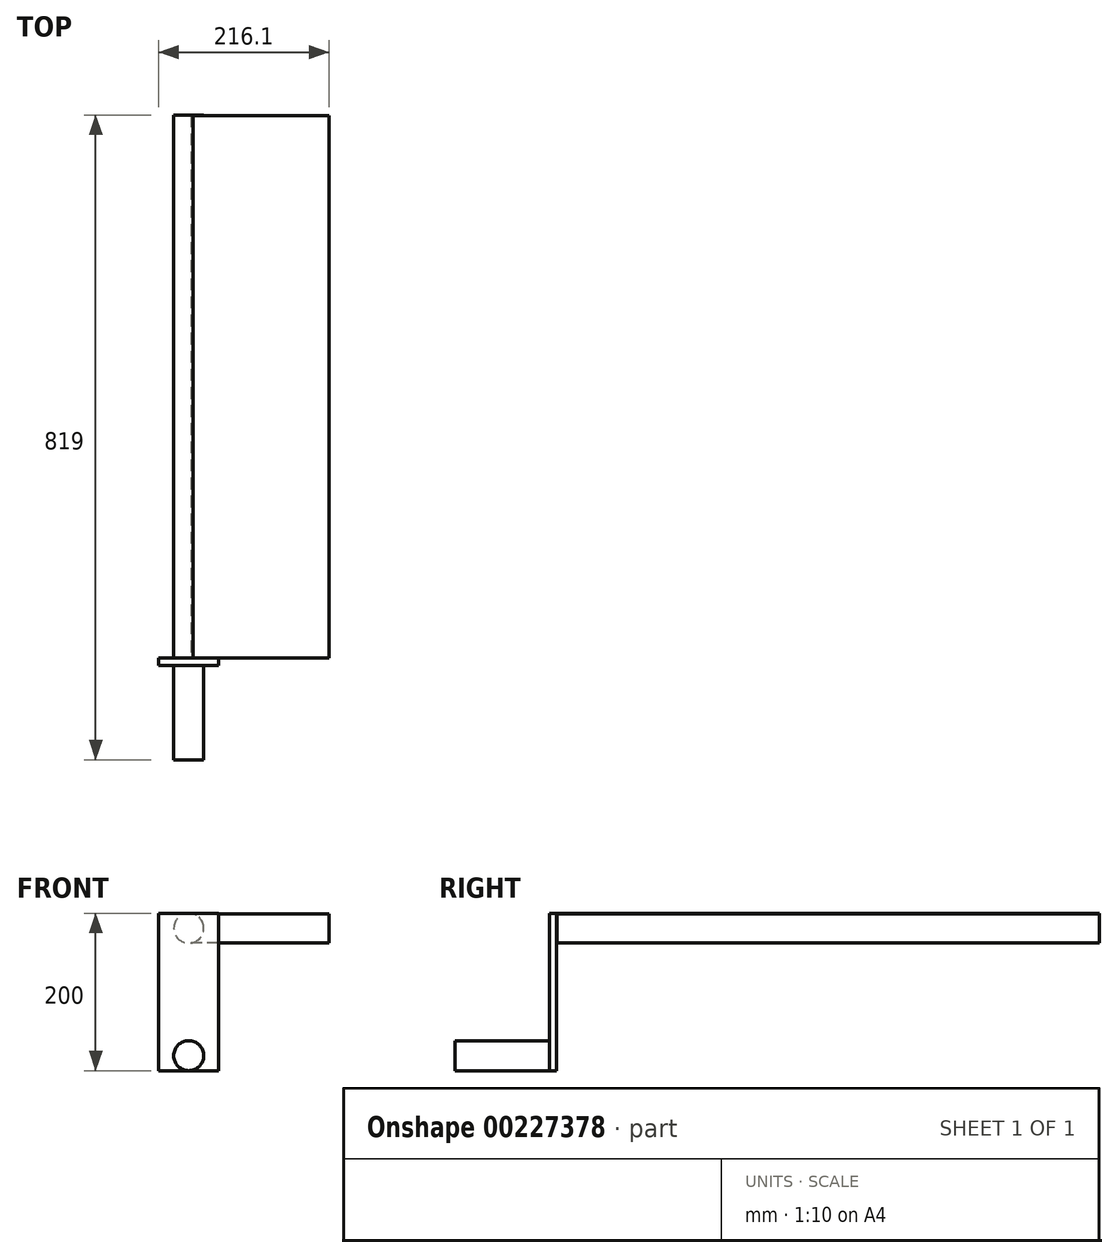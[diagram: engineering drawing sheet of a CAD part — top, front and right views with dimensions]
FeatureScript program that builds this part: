
annotation { "Feature Type Name" : "Feature", "Feature Type Description" : "" }
export const myFeature = defineFeature(function(context is Context, id is Id, definition is map)
    precondition{}
    {
        {
            var Q0;
            Q0=qCreatedBy(makeId("Front.planeOp"),FACE);
            var sketch = newSketch(context, id + "F0", { "sketchPlane" : qUnion([Q0])});
            skLineSegment(sketch, "E0.bottom", {"start": v(38.1, -100) * mm, "end": v(-38.1, -100) * mm});
            skLineSegment(sketch, "E0.top", {"start": v(38.1, 100) * mm, "end": v(-38.1, 100) * mm});
            skLineSegment(sketch, "E0.left", {"start": v(38.1, -100) * mm, "end": v(38.1, 100) * mm});
            skLineSegment(sketch, "E0.right", {"start": v(-38.1, -100) * mm, "end": v(-38.1, 100) * mm});
            skPoint(sketch, "E0.middle", {"position": v(0, 0) * mm});
            skSolve(sketch);
        }
        {
            var Q0;
            Q0 = qSketchRegion(id + "F0", true);
            extrude(context, id + "F1", {"entities" : qUnion([Q0]), "endBound" : BoundingType.SYMMETRIC, "depth" : 9 * mm});
        }
        {
            var Q0;
            Q0=makeQuery(id+"F1.opExtrude","CAP_FACE",FACE,{"disambiguationData":[OSD([sQuery(id+"F0.wireOp",EDGE,"E0.bottom"),sQuery(id+"F0.wireOp",EDGE,"E0.top"),sQuery(id+"F0.wireOp",EDGE,"E0.left"),sQuery(id+"F0.wireOp",EDGE,"E0.right")])],"isStart":false});
            var sketch = newSketch(context, id + "F2", { "sketchPlane" : qUnion([Q0])});
            skPoint(sketch, "E1.centerSnap0", {"position": v(0, -100) * mm});
            skCircle(sketch, "E2", {"center": v(0, -80.95) * mm, "radius": 19.05 * mm});
            skSolve(sketch);
        }
        {
            var Q0;
            Q0 = qSketchRegion(id + "F2", true);
            extrude(context, id + "F3", {"entities" : qUnion([Q0]), "operationType" : NewBodyOperationType.ADD, "depth" : 120 * mm});
        }
        {
            var Q0;
            Q0=makeQuery(id+"F1.opExtrude","CAP_FACE",FACE,{"disambiguationData":[OSD([sQuery(id+"F0.wireOp",EDGE,"E0.bottom"),sQuery(id+"F0.wireOp",EDGE,"E0.top"),sQuery(id+"F0.wireOp",EDGE,"E0.left"),sQuery(id+"F0.wireOp",EDGE,"E0.right")])],"isStart":true});
            var sketch = newSketch(context, id + "F4", { "sketchPlane" : qUnion([Q0])});
            skCircle(sketch, "E3", {"center": v(0, 81) * mm, "radius": 19 * mm});
            skPoint(sketch, "E3.centerSnap0", {"position": v(0, 100) * mm});
            skSolve(sketch);
        }
        {
            var Q0;
            Q0 = qSketchRegion(id + "F4", true);
            extrude(context, id + "F5", {"entities" : qUnion([Q0]), "operationType" : NewBodyOperationType.ADD, "depth" : 690 * mm});
        }
        {
            var Q0;
            Q0=qCreatedBy(makeId("Right.planeOp"),FACE);
            var sketch = newSketch(context, id + "F6", { "sketchPlane" : qUnion([Q0])});
            skLineSegment(sketch, "E4.bottom", {"start": v(5.02, 62.25) * mm, "end": v(693.98, 62.25) * mm});
            skLineSegment(sketch, "E4.top", {"start": v(5.02, 99.24) * mm, "end": v(693.98, 99.24) * mm});
            skLineSegment(sketch, "E4.left", {"start": v(5.02, 62.25) * mm, "end": v(5.02, 99.24) * mm});
            skLineSegment(sketch, "E4.right", {"start": v(693.98, 62.25) * mm, "end": v(693.98, 99.24) * mm});
            skSolve(sketch);
        }
        {
            var Q0;
            Q0 = qSketchRegion(id + "F6", true);
            extrude(context, id + "F7", {"entities" : qUnion([Q0]), "operationType" : NewBodyOperationType.ADD, "depth" : 178 * mm});
        }
    });
